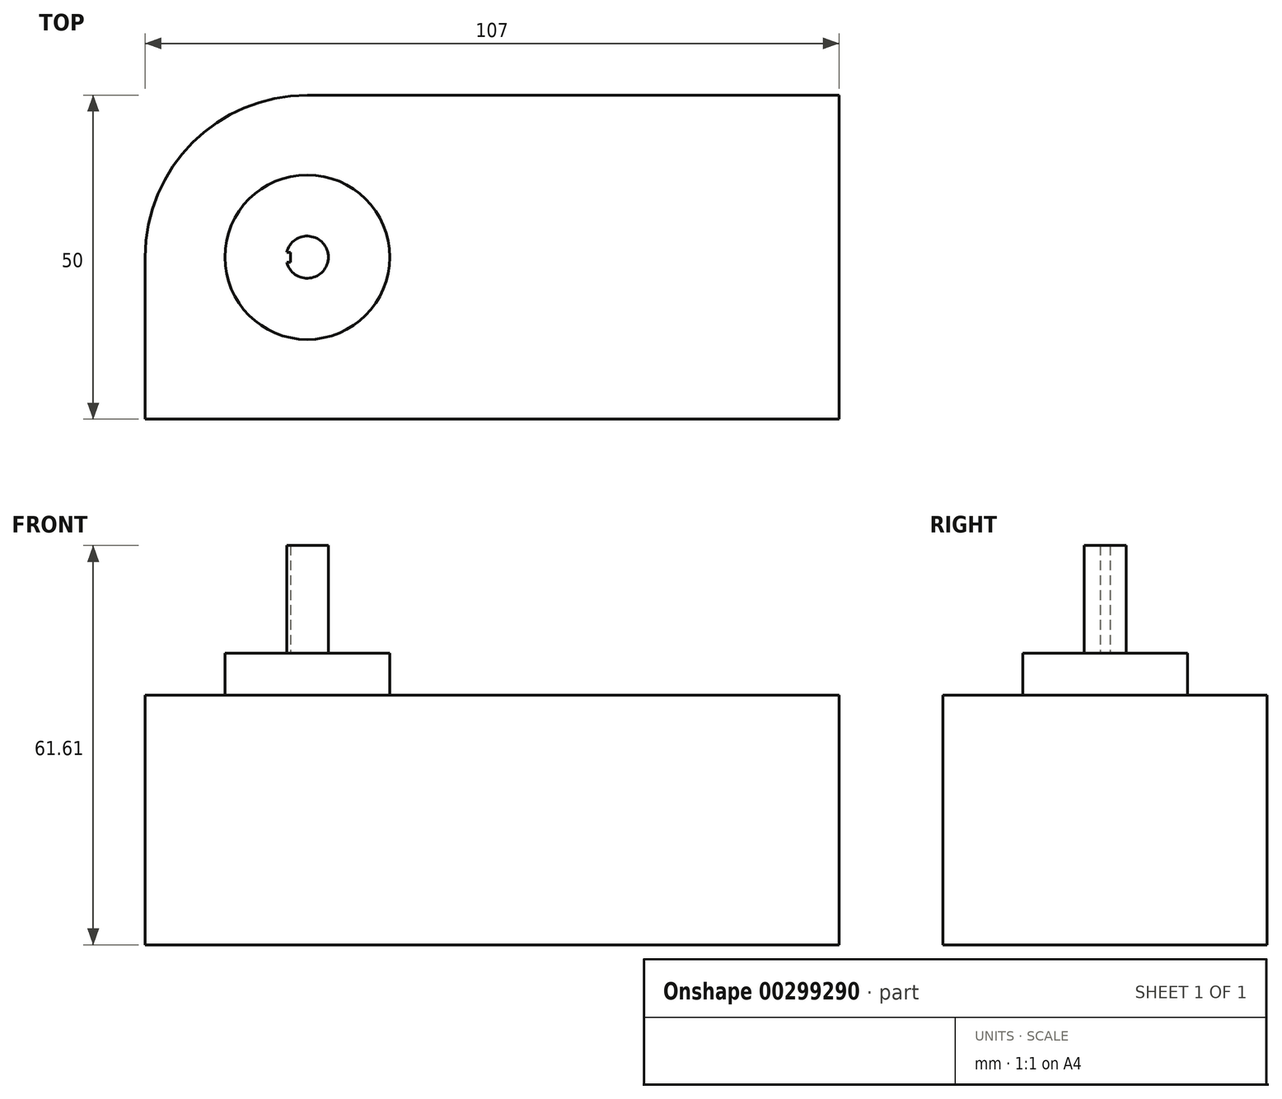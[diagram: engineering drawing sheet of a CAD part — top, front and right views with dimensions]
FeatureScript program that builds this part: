
annotation { "Feature Type Name" : "Feature", "Feature Type Description" : "" }
export const myFeature = defineFeature(function(context is Context, id is Id, definition is map)
    precondition{}
    {
        {
            var Q0;
            Q0=qCreatedBy(makeId("Top.planeOp"),FACE);
            var sketch = newSketch(context, id + "F0", { "sketchPlane" : qUnion([Q0])});
            skLineSegment(sketch, "E0.bottom", {"start": v(53.5, 25) * mm, "end": v(-28.5, 25) * mm});
            skLineSegment(sketch, "E0.top", {"start": v(53.5, -25) * mm, "end": v(-53.5, -25) * mm});
            skLineSegment(sketch, "E0.left", {"start": v(53.5, 25) * mm, "end": v(53.5, -25) * mm});
            skLineSegment(sketch, "E0.right", {"start": v(-53.5, 0) * mm, "end": v(-53.5, -25) * mm});
            skPoint(sketch, "E0.middle", {"position": v(0, 0) * mm});
            skPoint(sketch, "E1.visualSharp", {"position": v(-53.5, 25) * mm});
            skArc(sketch, "E1.filletArc", {"start": v(-28.5, 25) * mm, "mid": v(-46.18, 17.68) * mm, "end": v(-53.5, 0) * mm});
            skCircle(sketch, "E2", {"center": v(-28.5, 0) * mm, "radius": 12.7 * mm});
            skCircle(sketch, "E3", {"center": v(-28.5, 0) * mm, "radius": 3.25 * mm});
            skLineSegment(sketch, "E4", {"start": v(-31.66, 0.76) * mm, "end": v(-31.1, 0.76) * mm});
            skLineSegment(sketch, "E5", {"start": v(-31.1, 0.76) * mm, "end": v(-31.1, -0.76) * mm});
            skLineSegment(sketch, "E6", {"start": v(-31.1, -0.76) * mm, "end": v(-31.66, -0.76) * mm});
            skSolve(sketch);
        }
        {
            var Q0;
            {var subQ0=sQuery(id+"F0.wireOp",EDGE,"E4");Q0=makeQuery(id+"F0.imprint","IMPRINT",FACE,{"disambiguationData":[TD([[makeQuery(id+"F0.imprint","IMPRINT",EDGE,{"derivedFrom":subQ0}),-1.0]])]});}
            var Q1;
            {var subQ0=sQuery(id+"F0.wireOp",EDGE,"E4");Q1=makeQuery(id+"F0.imprint","IMPRINT",FACE,{"disambiguationData":[TD([[makeQuery(id+"F0.imprint","IMPRINT",EDGE,{"derivedFrom":subQ0}),1.0]])]});}
            var Q2;
            Q2=makeQuery(id+"F0.imprint","IMPRINT",FACE,{"disambiguationData":[TD([[makeQuery(id+"F0.imprint","IMPRINT",EDGE,{"derivedFrom":sQuery(id+"F0.wireOp",EDGE,"E2")}),1.0]])]});
            var Q3;
            Q3=makeQuery(id+"F0.imprint","IMPRINT",FACE,{"disambiguationData":[TD([[makeQuery(id+"F0.imprint","IMPRINT",EDGE,{"derivedFrom":sQuery(id+"F0.wireOp",EDGE,"E0.bottom")}),1.0]])]});
            extrude(context, id + "F1", {"entities" : qUnion([Q0, Q1, Q2, Q3]), "oppositeDirection" : true, "depth" : 38.5 * mm});
        }
        {
            var Q0;
            {var subQ0=sQuery(id+"F0.wireOp",EDGE,"E4");Q0=makeQuery(id+"F0.imprint","IMPRINT",FACE,{"disambiguationData":[TD([[makeQuery(id+"F0.imprint","IMPRINT",EDGE,{"derivedFrom":subQ0}),1.0]])]});}
            var Q1;
            Q1=sQuery(id+"F0.wireOp",EDGE,"E3");
            extrude(context, id + "F2", {"entities" : qUnion([Q0]), "operationType" : NewBodyOperationType.ADD, "surfaceEntities" : qUnion([Q1]), "depth" : 23.1 * mm});
        }
        {
            var Q0;
            Q0=makeQuery(id+"F0.imprint","IMPRINT",FACE,{"disambiguationData":[TD([[makeQuery(id+"F0.imprint","IMPRINT",EDGE,{"derivedFrom":sQuery(id+"F0.wireOp",EDGE,"E2")}),1.0]])]});
            var Q1;
            {var subQ0=sQuery(id+"F0.wireOp",EDGE,"E4");Q1=makeQuery(id+"F0.imprint","IMPRINT",FACE,{"disambiguationData":[TD([[makeQuery(id+"F0.imprint","IMPRINT",EDGE,{"derivedFrom":subQ0}),-1.0]])]});}
            extrude(context, id + "F3", {"entities" : qUnion([Q0, Q1]), "operationType" : NewBodyOperationType.ADD, "depth" : 6.5 * mm});
        }
    });
